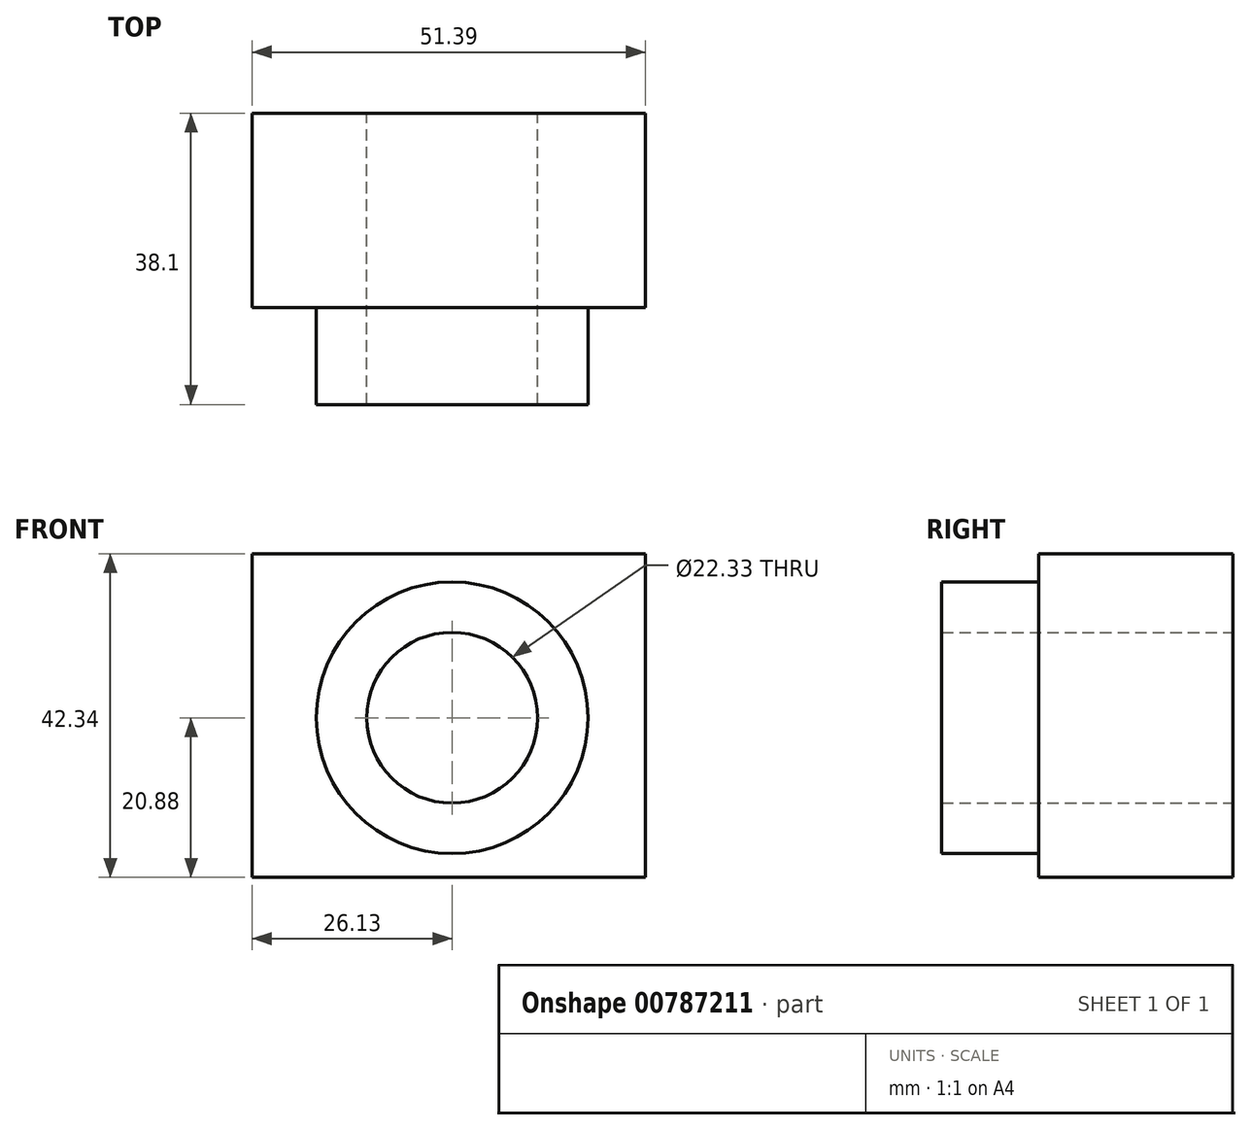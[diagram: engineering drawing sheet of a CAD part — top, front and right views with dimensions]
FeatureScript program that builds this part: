
annotation { "Feature Type Name" : "Feature", "Feature Type Description" : "" }
export const myFeature = defineFeature(function(context is Context, id is Id, definition is map)
    precondition{}
    {
        {
            var Q0;
            Q0=qCreatedBy(makeId("Front.planeOp"),FACE);
            var sketch = newSketch(context, id + "F0", { "sketchPlane" : qUnion([Q0])});
            skCircle(sketch, "E0", {"center": v(0, 0) * mm, "radius": 11.17 * mm});
            skCircle(sketch, "E1", {"center": v(0, 0) * mm, "radius": 17.76 * mm});
            skLineSegment(sketch, "E2.bottom", {"start": v(-26.13, -20.88) * mm, "end": v(25.26, -20.88) * mm});
            skLineSegment(sketch, "E2.top", {"start": v(-26.13, 21.46) * mm, "end": v(25.26, 21.46) * mm});
            skLineSegment(sketch, "E2.left", {"start": v(-26.13, -20.88) * mm, "end": v(-26.13, 21.46) * mm});
            skLineSegment(sketch, "E2.right", {"start": v(25.26, -20.88) * mm, "end": v(25.26, 21.46) * mm});
            skSolve(sketch);
        }
        {
            var Q0;
            Q0=makeQuery(id+"F0.imprint","IMPRINT",FACE,{"disambiguationData":[TD([[makeQuery(id+"F0.imprint","IMPRINT",EDGE,{"derivedFrom":sQuery(id+"F0.wireOp",EDGE,"E0")}),-1.0]])]});
            extrude(context, id + "F1", {"entities" : qUnion([Q0]), "depth" : 38.1 * mm, "offsetDistance" : 25.4 * mm});
        }
        {
            var Q0;
            Q0 = qSketchRegion(id + "F0", true);
            extrude(context, id + "F2", {"entities" : qUnion([Q0]), "operationType" : NewBodyOperationType.ADD, "depth" : 25.4 * mm, "offsetDistance" : 25.4 * mm});
        }
    });
